# Revit family: 1Drinking_Fountain-Haws_Corporation-Wall_Mounted_1119
name_source: partatom
category: Plumbing Fixtures
units: mm (PartAtom-declared; Revit-internal decimal feet)

## family parameters
Always vertical = Yes
Cut with Voids When Loaded = No
Host = Wall
OmniClass Number = 23.65.70.14.11
Part Type = Normal
Room Calculation Point = No
Round Connector Dimension = Use Radius
Shared = Yes

## types (1)
- Not a type, load type catalog!
    1920FR = Yes
    6521FR = Yes
    Apparent Load = 0 VA
    BP3 for 6521FR = Yes
    Back Panel = Metal - Haws Corporation - Satin Stainless Steel
    Bowl = Metal - Haws Corporation - Satin Stainless Steel
    Bowl Width = 15"
    CW Connection = Yes
    CWFU = 1
    Connector = 3
    Connector visibility = Yes
    Cost = $0
    Current = 0 A
    Default Elevation = 0"
    Electrical Connection Note = Electrical connection is only required for products that contain touchless sensors
    Flow = 0.00 GPM
    HW Connection = No
    HWFU = 0
    Manufacturer = Haws Corporation 1455 Kleppe Lane Sparks, NV 89431
    Nr = 3
    Nr 2 = 3
    Number of Poles = 1
    Power Factor = 1
    Sanitary Radius = 5/8"
    Sensor 1 = Yes
    Sensor 2 = Yes
    Supply Level = 28 5/8"
    Supply Radius = 1/4"
    Trim Plate = No
    Tubing = Metal - Haws Corporation - Copper Poly
    URL = http://www.hawsco.com
    VC = Yes
    Vent Connection = Yes
    Voltage = 0 V
    WC 1920FR = 3
    WC 6521FR = 3
    WFU = 0
    Waste Connection = No
    Waste Level = 31 1/8"

## geometry (parser evidence)
native form markers: Blend x16, Sweep x8
no freeform markers — native parametric forms only
